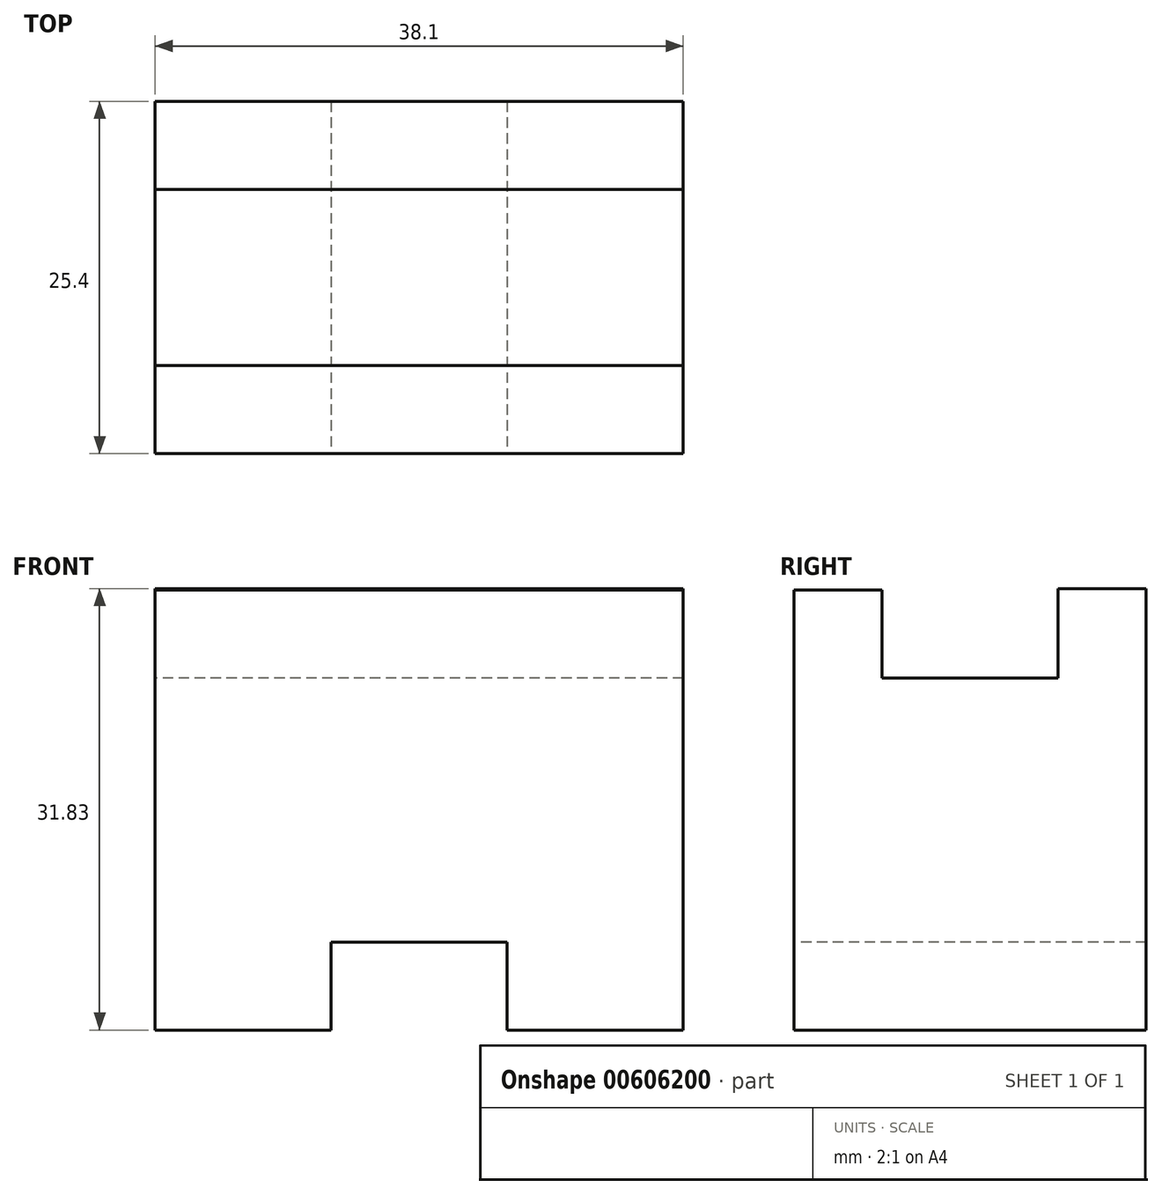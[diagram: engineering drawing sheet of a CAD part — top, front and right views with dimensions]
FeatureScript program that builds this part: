
annotation { "Feature Type Name" : "Feature", "Feature Type Description" : "" }
export const myFeature = defineFeature(function(context is Context, id is Id, definition is map)
    precondition{}
    {
        {
            var Q0;
            Q0=qCreatedBy(makeId("Right.planeOp"),FACE);
            var sketch = newSketch(context, id + "F0", { "sketchPlane" : qUnion([Q0])});
            skLineSegment(sketch, "E0", {"start": v(0, 0) * mm, "end": v(0, 31.75) * mm});
            skLineSegment(sketch, "E1", {"start": v(0, 31.75) * mm, "end": v(6.35, 31.75) * mm});
            skLineSegment(sketch, "E2", {"start": v(6.35, 31.75) * mm, "end": v(6.35, 25.4) * mm});
            skLineSegment(sketch, "E3", {"start": v(6.35, 25.4) * mm, "end": v(19.05, 25.4) * mm});
            skLineSegment(sketch, "E4", {"start": v(19.05, 25.4) * mm, "end": v(19.05, 31.83) * mm});
            skLineSegment(sketch, "E5", {"start": v(19.05, 31.83) * mm, "end": v(25.4, 31.83) * mm});
            skLineSegment(sketch, "E6", {"start": v(25.4, 31.83) * mm, "end": v(25.4, 0) * mm});
            skLineSegment(sketch, "E7", {"start": v(25.4, 0) * mm, "end": v(0, 0) * mm});
            skSolve(sketch);
        }
        {
            var Q0;
            Q0=makeQuery(id+"F0.imprint","IMPRINT",FACE,{"disambiguationData":[TD([[makeQuery(id+"F0.imprint","IMPRINT",EDGE,{"derivedFrom":sQuery(id+"F0.wireOp",EDGE,"E0")}),-1.0]])]});
            extrude(context, id + "F1", {"entities" : qUnion([Q0]), "depth" : 38.1 * mm, "offsetDistance" : 25.4 * mm});
        }
        {
            var Q0;
            Q0=makeQuery(id+"F1.opExtrude","SWEPT_FACE",FACE,{"disambiguationData":[OSD([sQuery(id+"F0.wireOp",EDGE,"E0")])]});
            var sketch = newSketch(context, id + "F2", { "sketchPlane" : qUnion([Q0])});
            skLineSegment(sketch, "E8", {"start": v(0, 0) * mm, "end": v(12.7, 0) * mm});
            skLineSegment(sketch, "E9", {"start": v(12.7, 0) * mm, "end": v(12.7, 6.35) * mm});
            skLineSegment(sketch, "E10", {"start": v(12.7, 6.35) * mm, "end": v(25.4, 6.35) * mm});
            skLineSegment(sketch, "E11", {"start": v(25.4, 6.35) * mm, "end": v(25.4, 0) * mm});
            skLineSegment(sketch, "E12", {"start": v(25.4, 0) * mm, "end": v(38.1, 0) * mm});
            skLineSegment(sketch, "E13", {"start": v(38.1, 0) * mm, "end": v(25.91, 0) * mm});
            skLineSegment(sketch, "E14", {"start": v(25.91, 0) * mm, "end": v(0, 0) * mm});
            skSolve(sketch);
        }
        {
            var Q0;
            {var subQ0=sQuery(id+"F2.wireOp",EDGE,"E9");Q0=makeQuery(id+"F2.imprint","IMPRINT",FACE,{"disambiguationData":[TD([[makeQuery(id+"F2.imprint","IMPRINT",EDGE,{"derivedFrom":subQ0}),-1.0]])]});}
            extrude(context, id + "F3", {"entities" : qUnion([Q0]), "operationType" : NewBodyOperationType.REMOVE, "oppositeDirection" : true, "depth" : 25.4 * mm, "offsetDistance" : 25.4 * mm});
        }
    });
